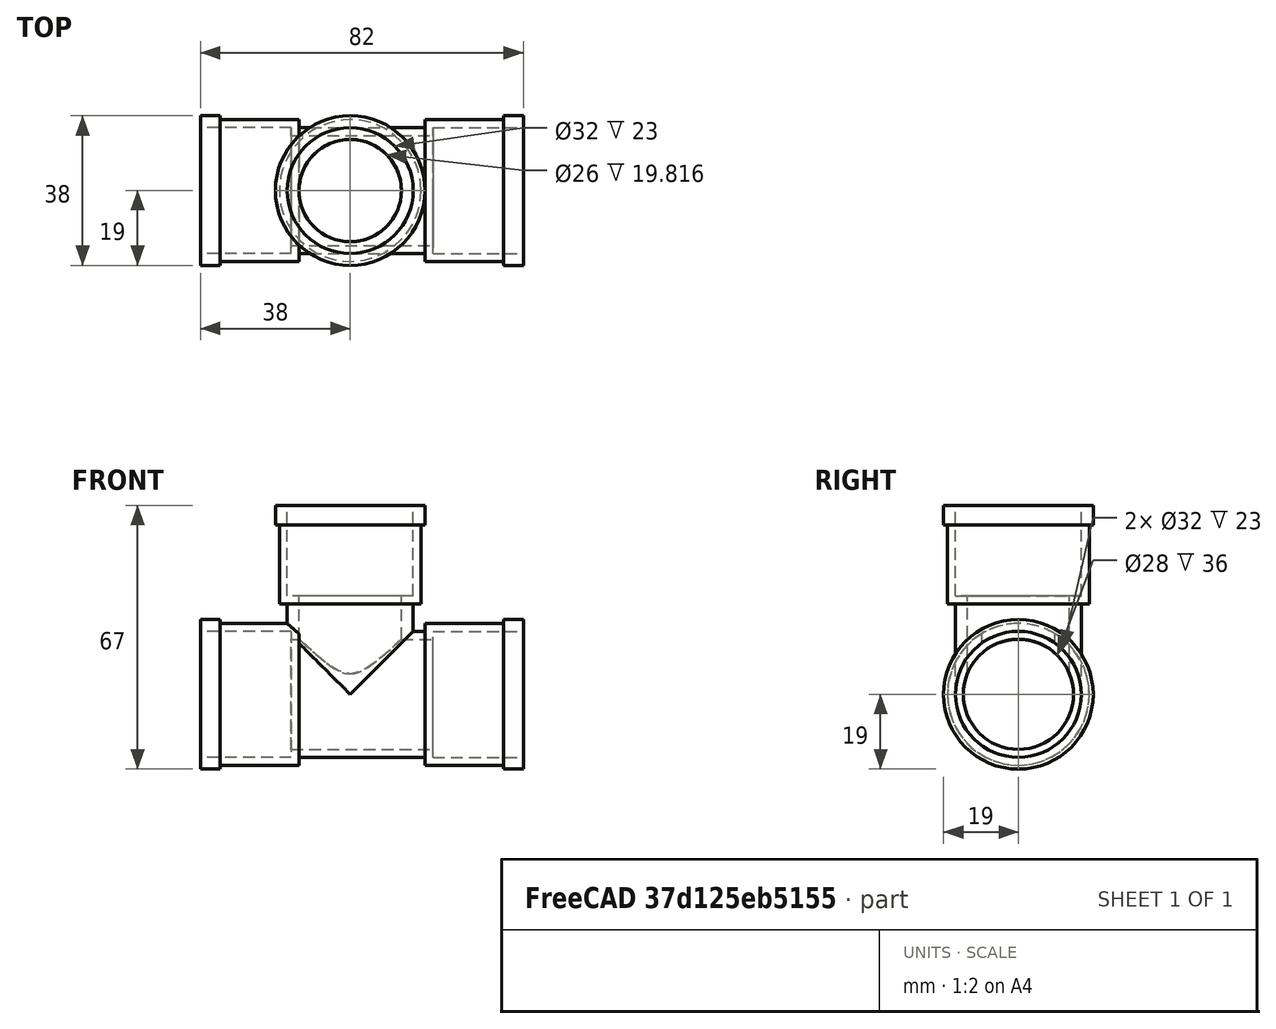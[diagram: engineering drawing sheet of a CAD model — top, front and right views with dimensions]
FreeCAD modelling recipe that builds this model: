
FCSTD DOCUMENT  (FreeCAD 0.16R6706 (Git))
Label: PVC Tee 32mm
License: CreativeCommons Attribution
LicenseURL: http://creativecommons.org/licenses/by/4.0/
objects: Part::Cylinder×13, Part::MultiFuse×7, Part::Cut×5
note: 25 computed .brp shape members not serialized (recipe doc carries the construction recipe); baked Part::Feature solids carry a one-line shape summary decoded from their .brp

FEATURE [Part::Cylinder] Cylinder144  label="Cilindro144"
  Angle = 360
  Height = 5
  Placement = pos=(0,0,20) rot=(0,0,1;0rad)
  Radius = 19
FEATURE [Part::Cylinder] Cylinder145  label="Cilindro145"
  Angle = 360
  Height = 20
  Radius = 18
FEATURE [Part::Cylinder] Cylinder146  label="taladro_T"
  Angle = 360
  Height = 24
  Placement = pos=(0,0,2) rot=(0,0,1;0rad)
  Radius = 16
FEATURE [Part::MultiFuse] Fusion065
  Shapes = -> [Cylinder144,Cylinder145]
FEATURE [Part::Cut] Cut091  label="Entrada_T"
  Base = -> Fusion065
  Placement = pos=(19,0,0) rot=(0,1,0;1.5708rad)
  Tool = -> Cylinder146
FEATURE [Part::Cylinder] Cylinder147  label="Cilindro146"
  Angle = 360
  Height = 5
  Placement = pos=(0,0,20) rot=(0,0,1;0rad)
  Radius = 19
FEATURE [Part::Cylinder] Cylinder148  label="Cilindro147"
  Angle = 360
  Height = 20
  Radius = 18
FEATURE [Part::Cylinder] Cylinder149  label="taladro_T001"
  Angle = 360
  Height = 24
  Placement = pos=(0,0,2) rot=(0,0,1;0rad)
  Radius = 16
FEATURE [Part::MultiFuse] Fusion066
  Shapes = -> [Cylinder147,Cylinder148]
FEATURE [Part::Cut] Cut092  label="Entrada_T001"
  Base = -> Fusion066
  Placement = pos=(0,0,23) rot=(0,0,1;0rad)
  Tool = -> Cylinder149
FEATURE [Part::Cylinder] Cylinder150  label="Cilindro148"
  Angle = 360
  Height = 23
  Radius = 16
FEATURE [Part::Cylinder] Cylinder151  label="Cilindro149"
  Angle = 360
  Height = 32
  Placement = pos=(-13,0,0) rot=(0,1,0;1.5708rad)
  Radius = 16
FEATURE [Part::MultiFuse] Fusion067
  Shapes = -> [Cut092,Cylinder150]
FEATURE [Part::Cylinder] Cylinder152  label="Cilindro150"
  Angle = 360
  Height = 5
  Placement = pos=(0,0,20) rot=(0,0,1;0rad)
  Radius = 19
FEATURE [Part::Cylinder] Cylinder153  label="Cilindro151"
  Angle = 360
  Height = 20
  Radius = 18
FEATURE [Part::Cylinder] Cylinder154  label="taladro_T002"
  Angle = 360
  Height = 24
  Placement = pos=(-15,0,0) rot=(0,-1,0;1.5708rad)
  Radius = 16
FEATURE [Part::MultiFuse] Fusion068
  Placement = pos=(-13,0,0) rot=(0,-1,0;1.5708rad)
  Shapes = -> [Cylinder152,Cylinder153]
FEATURE [Part::MultiFuse] Fusion069
  Shapes = -> [Cut091,Cylinder151]
FEATURE [Part::MultiFuse] Fusion070
  Shapes = -> [Fusion067,Fusion069]
FEATURE [Part::MultiFuse] Fusion071
  Shapes = -> [Fusion070,Fusion068]
FEATURE [Part::Cut] Cut093  label="Derivacion_T001"
  Base = -> Fusion071
  Tool = -> Cylinder154
FEATURE [Part::Cylinder] Cylinder  label="Cilindro"
  Angle = 360
  Height = 50
  Radius = 13
FEATURE [Part::Cut] Cut
  Base = -> Cut093
  Tool = -> Cylinder
FEATURE [Part::Cylinder] Cylinder155  label="Cilindro152"
  Angle = 360
  Height = 86
  Placement = pos=(-40,0,0) rot=(0,1,0;1.5708rad)
  Radius = 14
FEATURE [Part::Cut] Cut094  label="PVC Tee 32mm"
  Base = -> Cut
  Tool = -> Cylinder155
